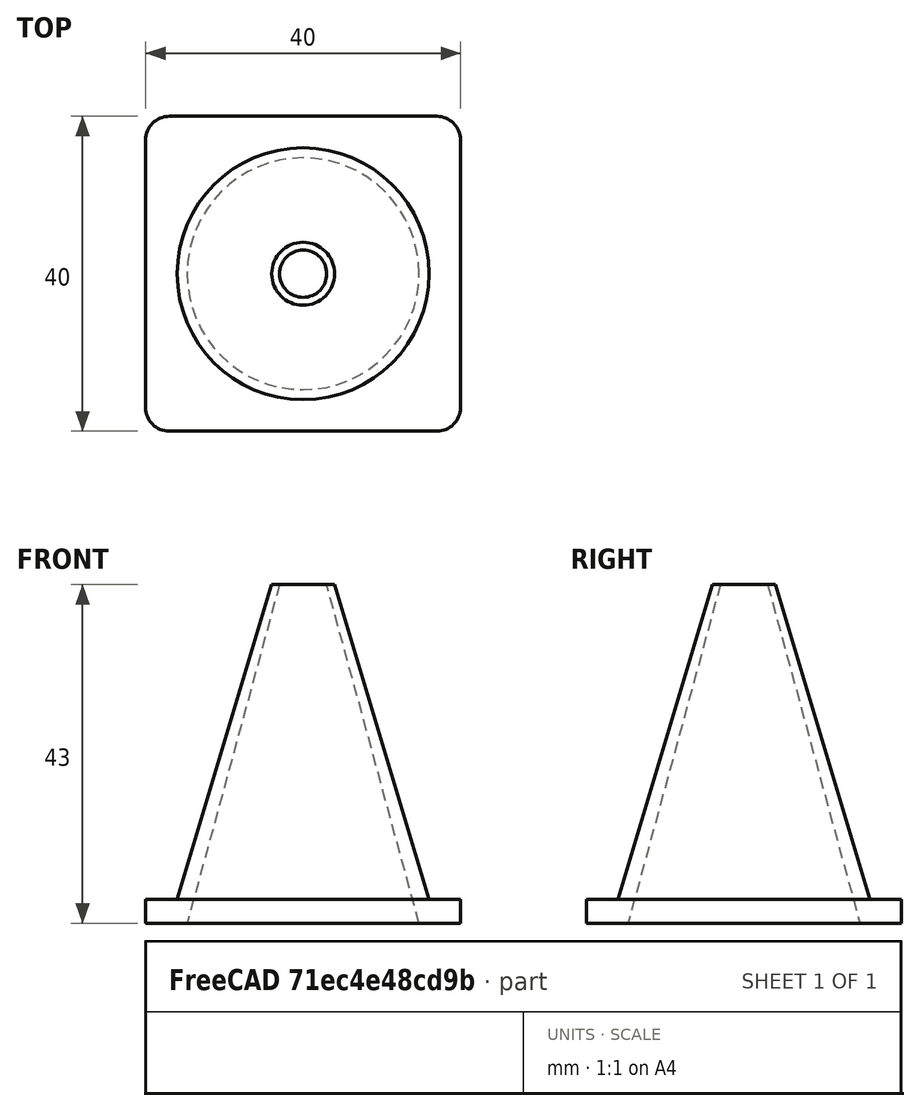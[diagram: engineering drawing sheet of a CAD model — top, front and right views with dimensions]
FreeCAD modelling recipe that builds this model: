
FCSTD DOCUMENT  (FreeCAD 0.21R33694 (Git))
Label: OJT1_T14R02.cono
License: All rights reserved
LicenseURL: http://en.wikipedia.org/wiki/All_rights_reserved
objects: Part::Cone×2, Part::Box×1, Part::Fillet×1, Part::Fuse×1, Part::Cut×1
note: 6 computed .brp shape members not serialized (recipe doc carries the construction recipe); baked Part::Feature solids carry a one-line shape summary decoded from their .brp

FEATURE [Part::Box] Box  label="Cub"
  AttacherType = Attacher::AttachEngine3D
  Height = 3
  Length = 40
  Width = 40
FEATURE [Part::Fillet] Fillet
  Base = -> Box
  Edges = 4 edges r=3: [Edge1,Edge3,Edge5,Edge7]
  Placement = pos=(-20,-20,-3) rot=(0,0,1;0rad)
FEATURE [Part::Cone] Cone  label="Con"
  Angle = 360
  AttacherType = Attacher::AttachEngine3D
  Height = 40
  Radius1 = 16
  Radius2 = 4
FEATURE [Part::Cone] Cone001  label="Con001"
  Angle = 360
  AttacherType = Attacher::AttachEngine3D
  Height = 44
  Placement = pos=(0,0,-4) rot=(0,0,1;0rad)
  Radius1 = 15
  Radius2 = 3
FEATURE [Part::Fuse] Fusion
  Base = -> Fillet
  Refine = true
  Tool = -> Cone
FEATURE [Part::Cut] Cut
  Base = -> Fusion
  Refine = true
  Tool = -> Cone001
